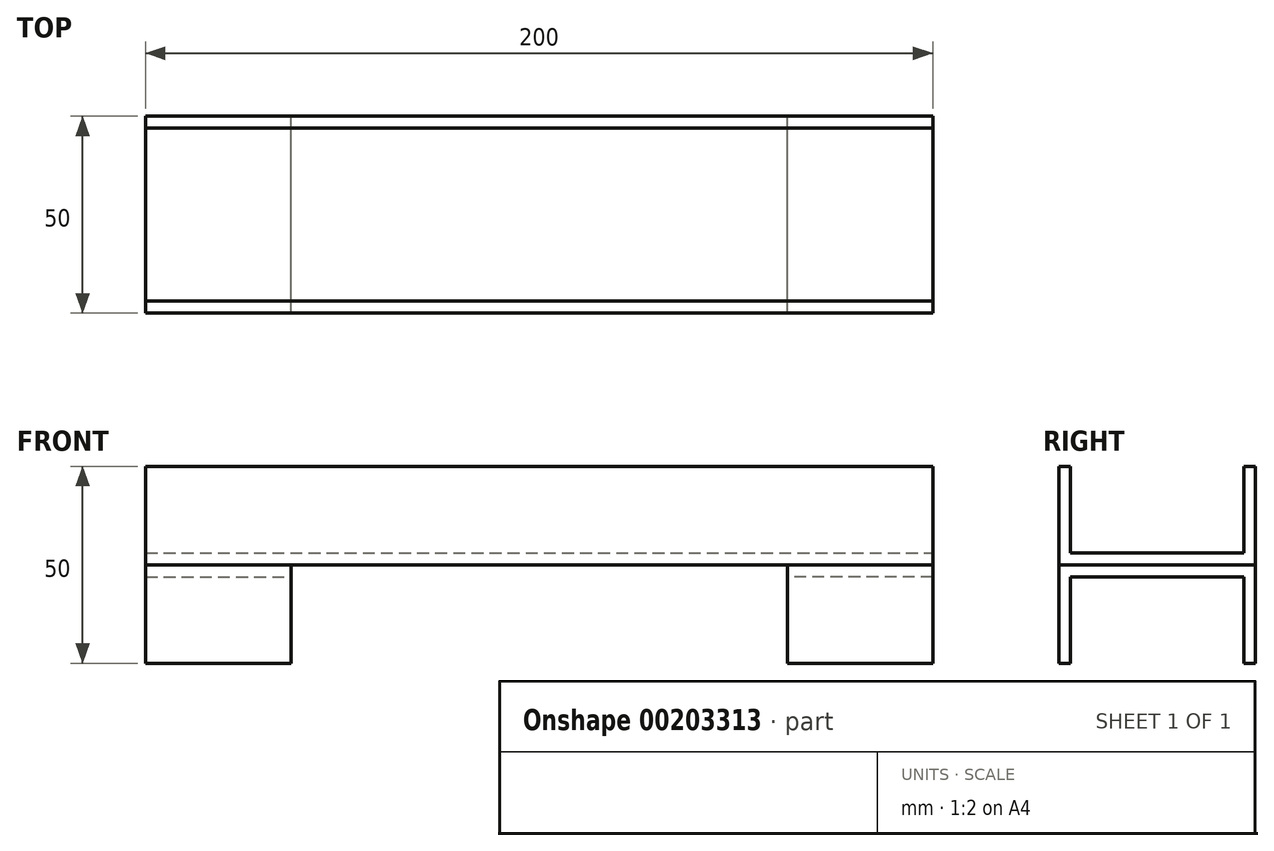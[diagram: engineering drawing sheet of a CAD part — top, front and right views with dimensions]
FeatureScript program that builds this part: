
annotation { "Feature Type Name" : "Feature", "Feature Type Description" : "" }
export const myFeature = defineFeature(function(context is Context, id is Id, definition is map)
    precondition{}
    {
        {
            var Q0;
            Q0=qCreatedBy(makeId("Front.planeOp"),FACE);
            var sketch = newSketch(context, id + "F0", { "sketchPlane" : qUnion([Q0])});
            skLineSegment(sketch, "E0.bottom", {"start": v(100, 12.5) * mm, "end": v(-100, 12.5) * mm});
            skLineSegment(sketch, "E0.top", {"start": v(100, -12.5) * mm, "end": v(-100, -12.5) * mm});
            skLineSegment(sketch, "E0.left", {"start": v(100, 12.5) * mm, "end": v(100, -12.5) * mm});
            skLineSegment(sketch, "E0.right", {"start": v(-100, 12.5) * mm, "end": v(-100, -12.5) * mm});
            skPoint(sketch, "E0.middle", {"position": v(0, 0) * mm});
            skSolve(sketch);
        }
        {
            var Q0;
            Q0 = qSketchRegion(id + "F0", true);
            extrude(context, id + "F1", {"entities" : qUnion([Q0]), "depth" : 50 * mm});
        }
        {
            var Q0;
            Q0=makeQuery(id+"F1.opExtrude","SWEPT_FACE",FACE,{"disambiguationData":[OSD([sQuery(id+"F0.wireOp",EDGE,"E0.left")])]});
            var sketch = newSketch(context, id + "F2", { "sketchPlane" : qUnion([Q0])});
            skLineSegment(sketch, "E1.bottom", {"start": v(-47, 12.5) * mm, "end": v(-3, 12.5) * mm});
            skLineSegment(sketch, "E1.top", {"start": v(-47, -9.5) * mm, "end": v(-3, -9.5) * mm});
            skLineSegment(sketch, "E1.left", {"start": v(-47, 12.5) * mm, "end": v(-47, -9.5) * mm});
            skLineSegment(sketch, "E1.right", {"start": v(-3, 12.5) * mm, "end": v(-3, -9.5) * mm});
            skLineSegment(sketch, "E2", {"start": v(-47, 7.32) * mm, "end": v(-50, 7.32) * mm, "construction": true});
            skLineSegment(sketch, "E3", {"start": v(-11.62, -9.5) * mm, "end": v(-11.62, -12.5) * mm, "construction": true});
            skLineSegment(sketch, "E4", {"start": v(-3, 1.5) * mm, "end": v(0, 1.5) * mm, "construction": true});
            skSolve(sketch);
        }
        {
            var Q0;
            Q0 = qSketchRegion(id + "F2", true);
            extrude(context, id + "F3", {"entities" : qUnion([Q0]), "operationType" : NewBodyOperationType.REMOVE, "endBound" : BoundingType.THROUGH_ALL, "oppositeDirection" : true, "depth" : 200 * mm});
        }
        {
            var Q0;
            Q0=makeQuery(id+"F1.opExtrude","SWEPT_FACE",FACE,{"disambiguationData":[OSD([sQuery(id+"F0.wireOp",EDGE,"E0.top")])]});
            var sketch = newSketch(context, id + "F4", { "sketchPlane" : qUnion([Q0])});
            skLineSegment(sketch, "E5.bottom", {"start": v(-63.04, 50) * mm, "end": v(-100, 50) * mm});
            skLineSegment(sketch, "E5.top", {"start": v(-63.04, 0) * mm, "end": v(-100, 0) * mm});
            skLineSegment(sketch, "E5.left", {"start": v(-63.04, 50) * mm, "end": v(-63.04, 0) * mm});
            skLineSegment(sketch, "E5.right", {"start": v(-100, 50) * mm, "end": v(-100, 0) * mm});
            skSolve(sketch);
        }
        {
            var Q0;
            Q0 = qSketchRegion(id + "F4", true);
            extrude(context, id + "F5", {"entities" : qUnion([Q0]), "depth" : 25 * mm});
        }
        {
            var Q0;
            Q0=makeQuery(id+"F5.opExtrude","SWEPT_FACE",FACE,{"disambiguationData":[OSD([sQuery(id+"F4.wireOp",EDGE,"E5.left")])]});
            var sketch = newSketch(context, id + "F6", { "sketchPlane" : qUnion([Q0])});
            skLineSegment(sketch, "E6.bottom", {"start": v(-47, -37.5) * mm, "end": v(-3, -37.5) * mm});
            skLineSegment(sketch, "E6.top", {"start": v(-47, -15.5) * mm, "end": v(-3, -15.5) * mm});
            skLineSegment(sketch, "E6.left", {"start": v(-47, -37.5) * mm, "end": v(-47, -15.5) * mm});
            skLineSegment(sketch, "E6.right", {"start": v(-3, -37.5) * mm, "end": v(-3, -15.5) * mm});
            skLineSegment(sketch, "E7", {"start": v(-47, -25.6) * mm, "end": v(-50, -25.6) * mm, "construction": true});
            skLineSegment(sketch, "E8", {"start": v(-27.97, -15.5) * mm, "end": v(-27.97, -12.5) * mm, "construction": true});
            skLineSegment(sketch, "E9", {"start": v(-3, -20.87) * mm, "end": v(0, -20.87) * mm, "construction": true});
            skSolve(sketch);
        }
        {
            var Q0;
            Q0=makeQuery(id+"F6.imprint","IMPRINT",FACE,{"disambiguationData":[TD([[makeQuery(id+"F6.imprint","IMPRINT",EDGE,{"derivedFrom":sQuery(id+"F6.wireOp",EDGE,"E6.bottom")}),1.0]])]});
            extrude(context, id + "F7", {"entities" : qUnion([Q0]), "operationType" : NewBodyOperationType.REMOVE, "endBound" : BoundingType.THROUGH_ALL, "oppositeDirection" : true, "depth" : 25 * mm});
        }
        {
            var Q0;
            Q0=makeQuery(id+"F5.opExtrude","SWEPT_BODY",BODY,{"disambiguationData":[OSD([sQuery(id+"F4.wireOp",EDGE,"E5.bottom"),sQuery(id+"F4.wireOp",EDGE,"E5.top"),sQuery(id+"F4.wireOp",EDGE,"E5.left"),sQuery(id+"F4.wireOp",EDGE,"E5.right")])]});
            var Q1;
            Q1=qCreatedBy(makeId("Right.planeOp"),FACE);
            mirror(context, id + "F8", {"entities" : qUnion([Q0]), "mirrorPlane" : qUnion([Q1])});
        }
    });
